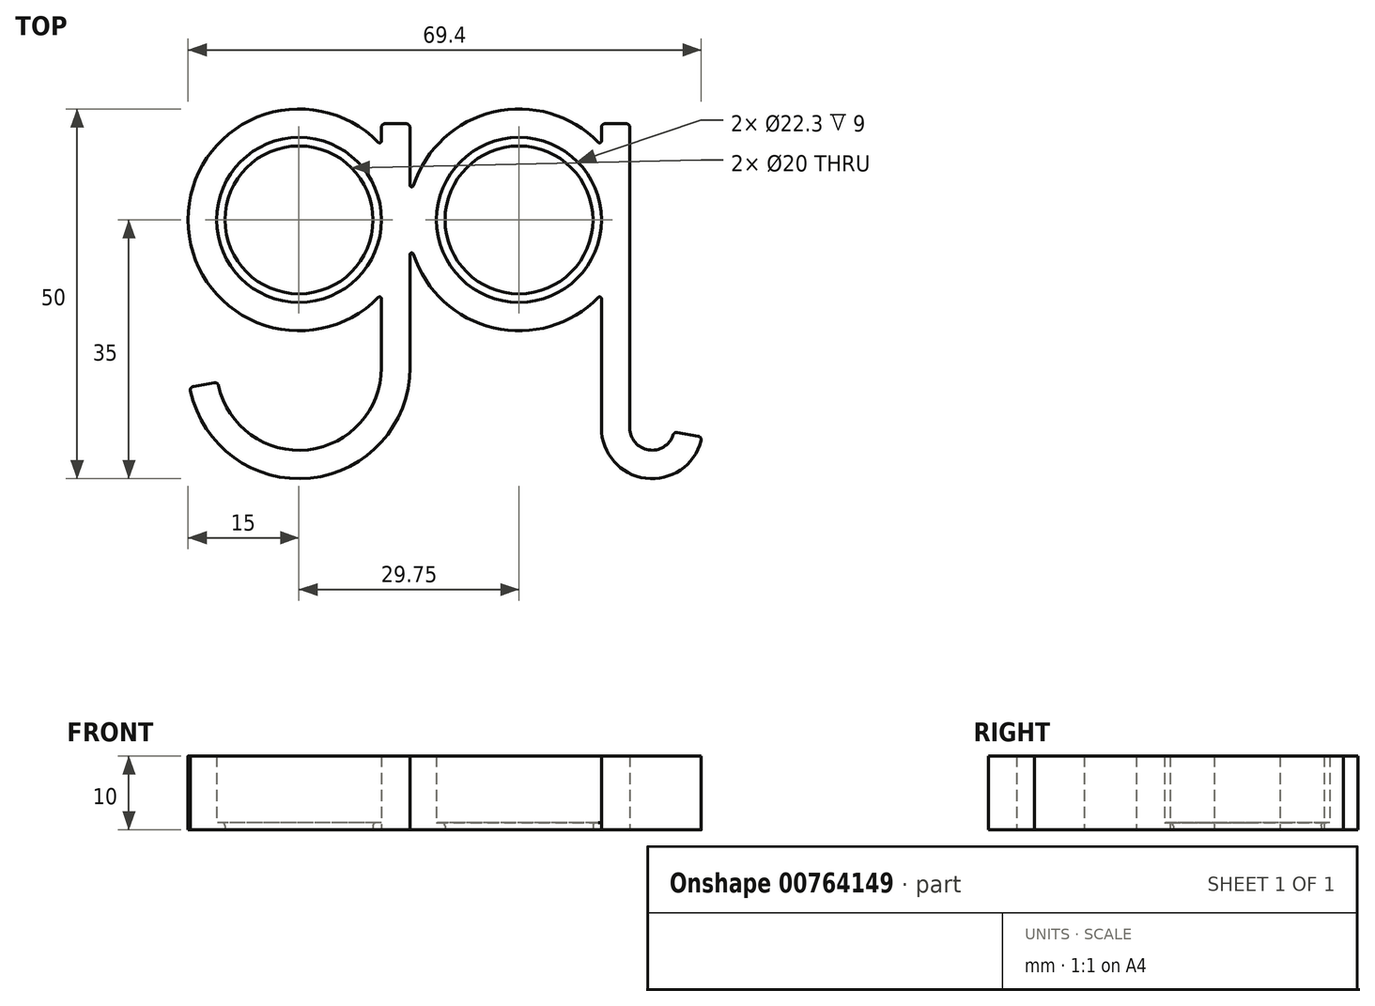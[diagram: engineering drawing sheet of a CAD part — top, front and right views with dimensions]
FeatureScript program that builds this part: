
annotation { "Feature Type Name" : "Feature", "Feature Type Description" : "" }
export const myFeature = defineFeature(function(context is Context, id is Id, definition is map)
    precondition{}
    {
        {
            var Q0;
            Q0=qCreatedBy(makeId("Top.planeOp"),FACE);
            var sketch = newSketch(context, id + "F0", { "sketchPlane" : qUnion([Q0])});
            skCircle(sketch, "E0", {"center": v(0, 0) * mm, "radius": 11.15 * mm});
            skArc(sketch, "E1", {"start": v(15, 0) * mm, "mid": v(-14, 5.37) * mm, "end": v(11.15, -10.03) * mm});
            skLineSegment(sketch, "E2", {"start": v(15, 0) * mm, "end": v(15, -20) * mm});
            skLineSegment(sketch, "E3", {"start": v(11.15, -10.03) * mm, "end": v(11.15, -20) * mm});
            skArc(sketch, "E4", {"start": v(-14.77, -22.6) * mm, "mid": v(1.3, -34.94) * mm, "end": v(15, -20) * mm});
            skLineSegment(sketch, "E5", {"start": v(15, -20) * mm, "end": v(11.15, -20) * mm, "construction": true});
            skArc(sketch, "E6", {"start": v(-10.98, -21.94) * mm, "mid": v(0.97, -31.1) * mm, "end": v(11.15, -20) * mm});
            skLineSegment(sketch, "E7", {"start": v(11.15, -20) * mm, "end": v(0, -20) * mm, "construction": true});
            skLineSegment(sketch, "E8", {"start": v(-10.98, -21.94) * mm, "end": v(-14.77, -22.6) * mm});
            skLineSegment(sketch, "E9", {"start": v(-10.98, -21.94) * mm, "end": v(0, -20) * mm, "construction": true});
            skPoint(sketch, "E10.orphan", {"position": v(11.15, 0) * mm});
            skLineSegment(sketch, "E11", {"start": v(15, 0) * mm, "end": v(15, 13) * mm});
            skLineSegment(sketch, "E12", {"start": v(15, 13) * mm, "end": v(11.15, 13) * mm});
            skLineSegment(sketch, "E13", {"start": v(11.15, 13) * mm, "end": v(11.15, 0) * mm});
            skCircle(sketch, "E14", {"center": v(29.75, 0) * mm, "radius": 11.15 * mm});
            skLineSegment(sketch, "E15", {"start": v(0, 0) * mm, "end": v(29.75, 0) * mm, "construction": true});
            skCircle(sketch, "E16", {"center": v(29.75, 0) * mm, "radius": 15 * mm});
            skLineSegment(sketch, "E17", {"start": v(40.9, 0) * mm, "end": v(40.9, 13) * mm});
            skLineSegment(sketch, "E18", {"start": v(40.9, 13) * mm, "end": v(44.75, 13) * mm});
            skLineSegment(sketch, "E19", {"start": v(44.75, 13) * mm, "end": v(44.75, -28.15) * mm});
            skLineSegment(sketch, "E20", {"start": v(44.75, -28.15) * mm, "end": v(40.9, -28.15) * mm});
            skLineSegment(sketch, "E21", {"start": v(40.9, -28.15) * mm, "end": v(40.9, 0) * mm});
            skLineSegment(sketch, "E22", {"start": v(44.75, -28.15) * mm, "end": v(47.75, -28.15) * mm, "construction": true});
            skArc(sketch, "E23", {"start": v(44.75, -28.15) * mm, "mid": v(47.49, -31.14) * mm, "end": v(50.7, -28.67) * mm});
            skArc(sketch, "E24", {"start": v(40.9, -28.15) * mm, "mid": v(47.15, -34.97) * mm, "end": v(54.5, -29.34) * mm});
            skLineSegment(sketch, "E25", {"start": v(47.75, -28.15) * mm, "end": v(54.5, -29.34) * mm, "construction": true});
            skLineSegment(sketch, "E26", {"start": v(50.7, -28.67) * mm, "end": v(54.5, -29.34) * mm});
            skLineSegment(sketch, "E27", {"start": v(0, -35) * mm, "end": v(47.75, -35) * mm, "construction": true});
            skLineSegment(sketch, "E28", {"start": v(47.75, -28.15) * mm, "end": v(47.75, -35) * mm, "construction": true});
            skSolve(sketch);
        }
        {
            var Q0;
            Q0=makeQuery(id+"F0.imprint","IMPRINT",FACE,{"disambiguationData":[TD([[makeQuery(id+"F0.imprint","IMPRINT",EDGE,{"derivedFrom":sQuery(id+"F0.wireOp",EDGE,"E0")}),-1.0]])]});
            var Q1;
            {var subQ0=sQuery(id+"F0.wireOp",EDGE,"E11");Q1=makeQuery(id+"F0.imprint","IMPRINT",FACE,{"disambiguationData":[TD([[makeQuery(id+"F0.imprint","IMPRINT",EDGE,{"derivedFrom":subQ0}),1.0]])]});}
            var Q2;
            {var subQ1=sQuery(id+"F0.wireOp",EDGE,"E12");Q2=makeQuery(id+"F0.imprint","IMPRINT",FACE,{"disambiguationData":[TD([[makeQuery(id+"F0.imprint","IMPRINT",EDGE,{"derivedFrom":subQ1}),1.0]])]});}
            var Q3;
            {var subQ8=sQuery(id+"F0.wireOp",EDGE,"E14");Q3=makeQuery(id+"F0.imprint","IMPRINT",FACE,{"disambiguationData":[TD([[makeQuery(id+"F0.imprint","IMPRINT",EDGE,{"derivedFrom":subQ8}),-1.0]])]});}
            var Q4;
            {var subQ0=sQuery(id+"F0.wireOp",EDGE,"E2");var subQ3=sQuery(id+"F0.wireOp",EDGE,"E16");var subQ5=makeQuery(id+"F0.imprint","INTERSECT",VERTEX,{"derivedFrom":[subQ0,subQ3]});Q4=makeQuery(id+"F0.imprint","IMPRINT",FACE,{"disambiguationData":[TD([[makeQuery(id+"F0.imprint","IMPRINT",EDGE,{"disambiguationData":[TD([[subQ5,1.0]])],"derivedFrom":subQ3}),1.0]])]});}
            var Q5;
            {var subQ0=sQuery(id+"F0.wireOp",EDGE,"E17");var subQ1=sQuery(id+"F0.wireOp",EDGE,"E16");var subQ2=makeQuery(id+"F0.imprint","INTERSECT",VERTEX,{"derivedFrom":[subQ1,subQ0]});Q5=makeQuery(id+"F0.imprint","IMPRINT",FACE,{"disambiguationData":[TD([[makeQuery(id+"F0.imprint","IMPRINT",EDGE,{"disambiguationData":[TD([[subQ2,1.0]])],"derivedFrom":subQ1}),1.0]])]});}
            var Q6;
            {var subQ5=sQuery(id+"F0.wireOp",EDGE,"E18");Q6=makeQuery(id+"F0.imprint","IMPRINT",FACE,{"disambiguationData":[TD([[makeQuery(id+"F0.imprint","IMPRINT",EDGE,{"derivedFrom":subQ5}),-1.0]])]});}
            var Q7;
            {var subQ5=sQuery(id+"F0.wireOp",EDGE,"E20");Q7=makeQuery(id+"F0.imprint","IMPRINT",FACE,{"disambiguationData":[TD([[makeQuery(id+"F0.imprint","IMPRINT",EDGE,{"derivedFrom":subQ5}),-1.0]])]});}
            var Q8;
            Q8=makeQuery(id+"F0.imprint","IMPRINT",FACE,{"disambiguationData":[TD([[makeQuery(id+"F0.imprint","IMPRINT",EDGE,{"derivedFrom":sQuery(id+"F0.wireOp",EDGE,"E20")}),1.0]])]});
            extrude(context, id + "F1", {"entities" : qUnion([Q0, Q1, Q2, Q3, Q4, Q5, Q6, Q7, Q8]), "depth" : 10 * mm, "offsetDistance" : 25 * mm});
        }
        {
            var Q0;
            Q0=qCreatedBy(makeId("Top.planeOp"),FACE);
            var sketch = newSketch(context, id + "F2", { "sketchPlane" : qUnion([Q0])});
            skCircle(sketch, "E29", {"center": v(0, 0) * mm, "radius": 11.5 * mm});
            skCircle(sketch, "E30", {"center": v(0, 0) * mm, "radius": 10 * mm});
            skCircle(sketch, "E31.0", {"center": v(29.75, 0) * mm, "radius": 11.15 * mm, "construction": true});
            skCircle(sketch, "E32", {"center": v(29.75, 0) * mm, "radius": 10 * mm});
            skCircle(sketch, "E33", {"center": v(29.75, 0) * mm, "radius": 11.5 * mm});
            skSolve(sketch);
        }
        {
            var Q0;
            Q0 = qSketchRegion(id + "F2", true);
            extrude(context, id + "F3", {"entities" : qUnion([Q0]), "operationType" : NewBodyOperationType.ADD, "depth" : 1 * mm, "offsetDistance" : 25 * mm});
        }
        {
            var Q0;
            Q0=makeQuery(id+"F3.opExtrude","CAP_EDGE",EDGE,{"disambiguationData":[OSD([sQuery(id+"F2.wireOp",EDGE,"E30")])],"isStart":false});
            var Q1;
            Q1=makeQuery(id+"F3.opExtrude","CAP_EDGE",EDGE,{"disambiguationData":[OSD([sQuery(id+"F2.wireOp",EDGE,"E32")])],"isStart":false});
            fillet(context, id + "F4", {"entities" : qUnion([Q0, Q1]), "radius" : .5 * mm, "tangentPropagation" : true, "allowEdgeOverflow" : false});
        }
        {
            var Q0;
            Q0=makeQuery(id+"F1.opExtrude","SWEPT_EDGE",EDGE,{"disambiguationData":[OSD([sQuery(id+"F0.wireOp",EDGE,"E2"),sQuery(id+"F0.wireOp",EDGE,"E16")])]});
            var Q1;
            Q1=makeQuery(id+"F1.opExtrude","SWEPT_EDGE",EDGE,{"disambiguationData":[OSD([sQuery(id+"F0.wireOp",EDGE,"E11"),sQuery(id+"F0.wireOp",EDGE,"E16")])]});
            var Q2;
            Q2=makeQuery(id+"F1.opExtrude","SWEPT_EDGE",EDGE,{"disambiguationData":[OSD([sQuery(id+"F0.wireOp",EDGE,"E1"),sQuery(id+"F0.wireOp",EDGE,"E13")])]});
            var Q3;
            Q3=makeQuery(id+"F1.opExtrude","SWEPT_EDGE",EDGE,{"disambiguationData":[OSD([sQuery(id+"F0.wireOp",EDGE,"E16"),sQuery(id+"F0.wireOp",EDGE,"E17")])]});
            var Q4;
            Q4=makeQuery(id+"F1.opExtrude","SWEPT_EDGE",EDGE,{"disambiguationData":[OSD([sQuery(id+"F0.wireOp",EDGE,"E1"),sQuery(id+"F0.wireOp",EDGE,"E3")])]});
            var Q5;
            Q5=makeQuery(id+"F1.opExtrude","SWEPT_EDGE",EDGE,{"disambiguationData":[OSD([sQuery(id+"F0.wireOp",EDGE,"E16"),sQuery(id+"F0.wireOp",EDGE,"E21")])]});
            fillet(context, id + "F5", {"entities" : qUnion([Q0, Q1, Q2, Q3, Q4, Q5]), "radius" : .25 * mm, "tangentPropagation" : true, "allowEdgeOverflow" : false});
        }
        {
            var Q0;
            Q0=makeQuery(id+"F1.opExtrude","SWEPT_EDGE",EDGE,{"disambiguationData":[OSD([sQuery(id+"F0.wireOp",EDGE,"E6"),sQuery(id+"F0.wireOp",EDGE,"E8")])]});
            var Q1;
            Q1=makeQuery(id+"F1.opExtrude","SWEPT_EDGE",EDGE,{"disambiguationData":[OSD([sQuery(id+"F0.wireOp",EDGE,"E4"),sQuery(id+"F0.wireOp",EDGE,"E8")])]});
            var Q2;
            Q2=makeQuery(id+"F1.opExtrude","SWEPT_EDGE",EDGE,{"disambiguationData":[OSD([sQuery(id+"F0.wireOp",EDGE,"E12"),sQuery(id+"F0.wireOp",EDGE,"E13")])]});
            var Q3;
            Q3=makeQuery(id+"F1.opExtrude","SWEPT_EDGE",EDGE,{"disambiguationData":[OSD([sQuery(id+"F0.wireOp",EDGE,"E11"),sQuery(id+"F0.wireOp",EDGE,"E12")])]});
            var Q4;
            Q4=makeQuery(id+"F1.opExtrude","SWEPT_EDGE",EDGE,{"disambiguationData":[OSD([sQuery(id+"F0.wireOp",EDGE,"E17"),sQuery(id+"F0.wireOp",EDGE,"E18")])]});
            var Q5;
            Q5=makeQuery(id+"F1.opExtrude","SWEPT_EDGE",EDGE,{"disambiguationData":[OSD([sQuery(id+"F0.wireOp",EDGE,"E18"),sQuery(id+"F0.wireOp",EDGE,"E19")])]});
            var Q6;
            Q6=makeQuery(id+"F1.opExtrude","SWEPT_EDGE",EDGE,{"disambiguationData":[OSD([sQuery(id+"F0.wireOp",EDGE,"E24"),sQuery(id+"F0.wireOp",EDGE,"E26")])]});
            var Q7;
            Q7=makeQuery(id+"F1.opExtrude","SWEPT_EDGE",EDGE,{"disambiguationData":[OSD([sQuery(id+"F0.wireOp",EDGE,"E23"),sQuery(id+"F0.wireOp",EDGE,"E26")])]});
            fillet(context, id + "F6", {"entities" : qUnion([Q0, Q1, Q2, Q3, Q4, Q5, Q6, Q7]), "radius" : .5 * mm, "tangentPropagation" : true, "allowEdgeOverflow" : false});
        }
    });
